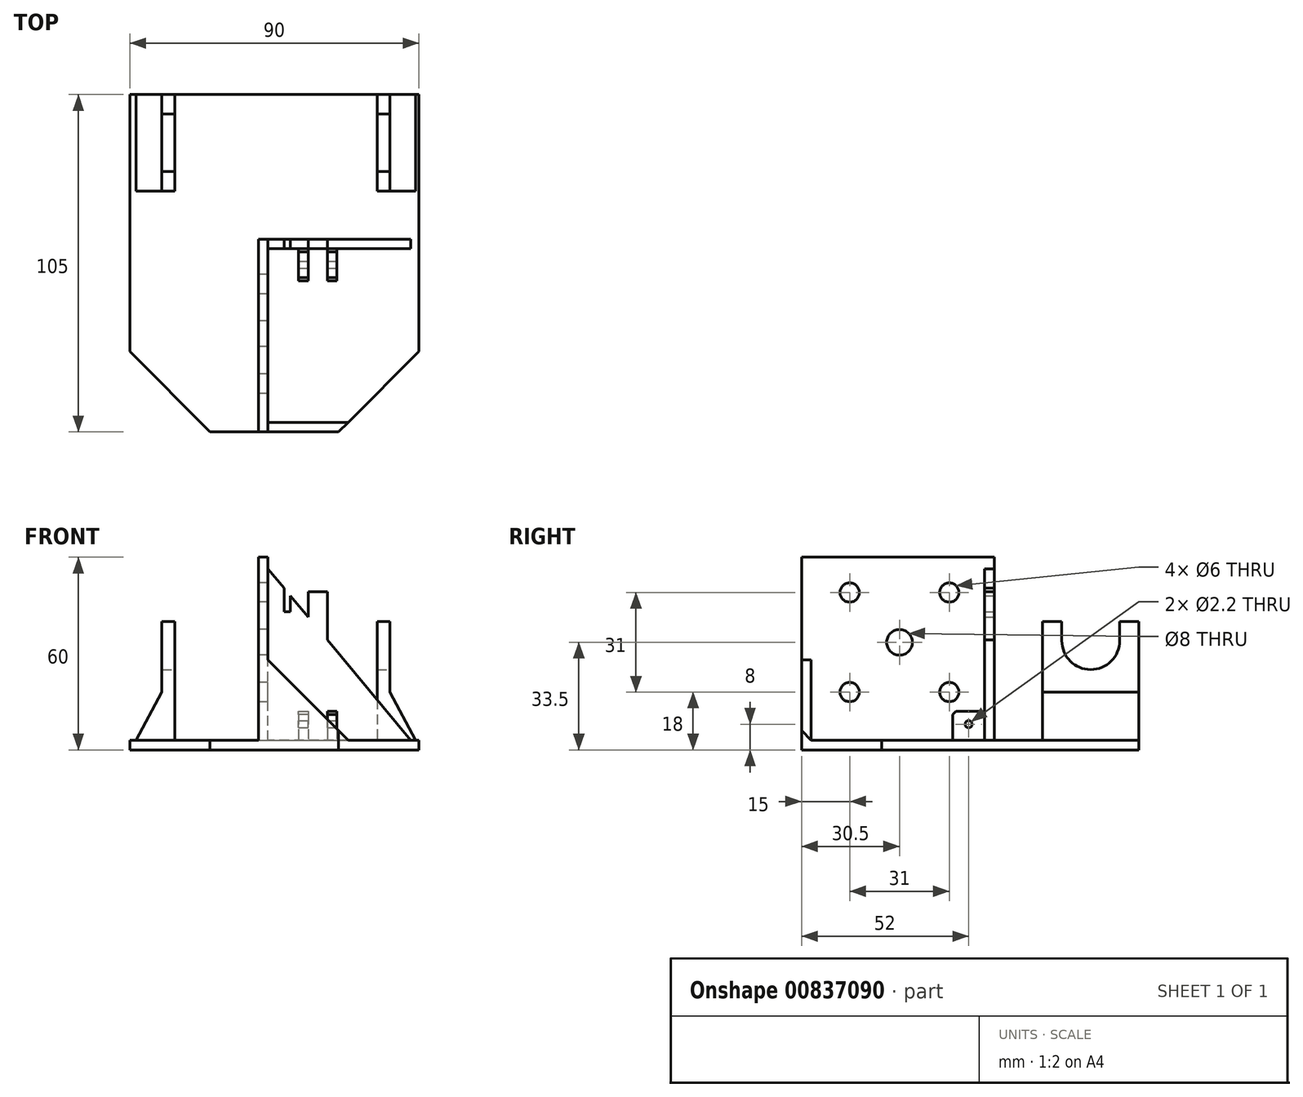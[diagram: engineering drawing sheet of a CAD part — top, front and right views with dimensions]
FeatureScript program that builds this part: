
annotation { "Feature Type Name" : "Feature", "Feature Type Description" : "" }
export const myFeature = defineFeature(function(context is Context, id is Id, definition is map)
    precondition{}
    {
        {
            var Q0;
            Q0=qCreatedBy(makeId("Top.planeOp"),FACE);
            var sketch = newSketch(context, id + "F0", { "sketchPlane" : qUnion([Q0])});
            skLineSegment(sketch, "E0.bottom", {"start": v(0, 0) * mm, "end": v(50, 0) * mm});
            skLineSegment(sketch, "E0.top", {"start": v(0, -60) * mm, "end": v(50, -60) * mm});
            skLineSegment(sketch, "E0.left", {"start": v(0, 0) * mm, "end": v(0, -60) * mm});
            skLineSegment(sketch, "E0.right", {"start": v(50, 0) * mm, "end": v(50, -60) * mm});
            skLineSegment(sketch, "E1.top", {"start": v(0, 45) * mm, "end": v(50, 45) * mm});
            skLineSegment(sketch, "E1.left", {"start": v(0, 0) * mm, "end": v(0, 45) * mm});
            skLineSegment(sketch, "E1.right", {"start": v(50, 0) * mm, "end": v(50, 45) * mm});
            skLineSegment(sketch, "E2.bottom", {"start": v(0, -60) * mm, "end": v(-40, -60) * mm});
            skLineSegment(sketch, "E2.top", {"start": v(0, 0) * mm, "end": v(-40, 0) * mm});
            skLineSegment(sketch, "E2.left", {"start": v(0, -60) * mm, "end": v(0, 0) * mm});
            skLineSegment(sketch, "E2.right", {"start": v(-40, -60) * mm, "end": v(-40, 0) * mm});
            skLineSegment(sketch, "E3.bottom", {"start": v(21.5, -3) * mm, "end": v(24.5, -3) * mm});
            skLineSegment(sketch, "E3.top", {"start": v(21.5, -13) * mm, "end": v(24.5, -13) * mm});
            skLineSegment(sketch, "E3.left", {"start": v(21.5, -3) * mm, "end": v(21.5, -13) * mm});
            skLineSegment(sketch, "E3.right", {"start": v(24.5, -3) * mm, "end": v(24.5, -13) * mm});
            skLineSegment(sketch, "E4.bottom", {"start": v(12.5, -3) * mm, "end": v(15.5, -3) * mm});
            skLineSegment(sketch, "E4.top", {"start": v(12.5, -13) * mm, "end": v(15.5, -13) * mm});
            skLineSegment(sketch, "E4.left", {"start": v(12.5, -3) * mm, "end": v(12.5, -13) * mm});
            skLineSegment(sketch, "E4.right", {"start": v(15.5, -3) * mm, "end": v(15.5, -13) * mm});
            skLineSegment(sketch, "E5", {"start": v(-40, 45) * mm, "end": v(-40, 0) * mm});
            skLineSegment(sketch, "E6", {"start": v(-40, 45) * mm, "end": v(0, 45) * mm});
            skLineSegment(sketch, "E7.bottom", {"start": v(-30, 45) * mm, "end": v(-26, 45) * mm});
            skLineSegment(sketch, "E7.top", {"start": v(-30, 15) * mm, "end": v(-26, 15) * mm});
            skLineSegment(sketch, "E7.left", {"start": v(-30, 45) * mm, "end": v(-30, 15) * mm});
            skLineSegment(sketch, "E7.right", {"start": v(-26, 45) * mm, "end": v(-26, 15) * mm});
            skLineSegment(sketch, "E8.bottom", {"start": v(37, 45) * mm, "end": v(41, 45) * mm});
            skLineSegment(sketch, "E8.top", {"start": v(37, 15) * mm, "end": v(41, 15) * mm});
            skLineSegment(sketch, "E8.left", {"start": v(37, 45) * mm, "end": v(37, 15) * mm});
            skLineSegment(sketch, "E8.right", {"start": v(41, 45) * mm, "end": v(41, 15) * mm});
            skSolve(sketch);
        }
        {
            var Q0;
            Q0=makeQuery(id+"F0.imprint","IMPRINT",FACE,{"disambiguationData":[TD([[makeQuery(id+"F0.imprint","IMPRINT",EDGE,{"derivedFrom":sQuery(id+"F0.wireOp",EDGE,"E0.left")}),-1.0]])]});
            var Q1;
            Q1=makeQuery(id+"F0.imprint","IMPRINT",FACE,{"disambiguationData":[TD([[makeQuery(id+"F0.imprint","IMPRINT",EDGE,{"derivedFrom":sQuery(id+"F0.wireOp",EDGE,"E0.bottom")}),-1.0]])]});
            var Q2;
            {var subQ1=sQuery(id+"F0.wireOp",EDGE,"48ikspD8-P3td-oRdJ-VHEi-jSUkpiZ7QIT4.bottom");Q2=makeQuery(id+"F0.imprint","IMPRINT",FACE,{"disambiguationData":[TD([[makeQuery(id+"F0.imprint","IMPRINT",EDGE,{"derivedFrom":subQ1}),-1.0]])]});}
            var Q3;
            Q3=makeQuery(id+"F0.imprint","IMPRINT",FACE,{"disambiguationData":[TD([[makeQuery(id+"F0.imprint","IMPRINT",EDGE,{"derivedFrom":sQuery(id+"F0.wireOp",EDGE,"E0.bottom")}),1.0]])]});
            var Q4;
            Q4=makeQuery(id+"F0.imprint","IMPRINT",FACE,{"disambiguationData":[TD([[makeQuery(id+"F0.imprint","IMPRINT",EDGE,{"derivedFrom":sQuery(id+"F0.wireOp",EDGE,"48ikspD8-P3td-oRdJ-VHEi-jSUkpiZ7QIT4.bottom")}),1.0]])]});
            var Q5;
            Q5=makeQuery(id+"F0.imprint","IMPRINT",FACE,{"disambiguationData":[TD([[makeQuery(id+"F0.imprint","IMPRINT",EDGE,{"derivedFrom":sQuery(id+"F0.wireOp",EDGE,"BPw0P3i8-2CSX-RIvv-VPia-wM2BSo4PSIyP.bottom")}),1.0]])]});
            var Q6;
            {var subQ2=sQuery(id+"F0.wireOp",EDGE,"BPw0P3i8-2CSX-RIvv-VPia-wM2BSo4PSIyP.bottom");Q6=makeQuery(id+"F0.imprint","IMPRINT",FACE,{"disambiguationData":[TD([[makeQuery(id+"F0.imprint","IMPRINT",EDGE,{"derivedFrom":subQ2}),-1.0]])]});}
            var Q7;
            {var subQ2=sQuery(id+"F0.wireOp",EDGE,"BPw0P3i8-2CSX-RIvv-VPia-wM2BSo4PSIyP.top");Q7=makeQuery(id+"F0.imprint","IMPRINT",FACE,{"disambiguationData":[TD([[makeQuery(id+"F0.imprint","IMPRINT",EDGE,{"derivedFrom":subQ2}),1.0]])]});}
            var Q8;
            {var subQ2=sQuery(id+"F0.wireOp",EDGE,"48ikspD8-P3td-oRdJ-VHEi-jSUkpiZ7QIT4.top");Q8=makeQuery(id+"F0.imprint","IMPRINT",FACE,{"disambiguationData":[TD([[makeQuery(id+"F0.imprint","IMPRINT",EDGE,{"derivedFrom":subQ2}),1.0]])]});}
            var Q9;
            {var subQ1=sQuery(id+"F0.wireOp",EDGE,"E1.left");Q9=makeQuery(id+"F0.imprint","IMPRINT",FACE,{"disambiguationData":[TD([[makeQuery(id+"F0.imprint","IMPRINT",EDGE,{"derivedFrom":subQ1}),1.0]])]});}
            extrude(context, id + "F1", {"entities" : qUnion([Q0, Q1, Q2, Q3, Q4, Q5, Q6, Q7, Q8, Q9]), "depth" : 3 * mm, "offsetDistance" : 25 * mm});
        }
        {
            var Q0;
            Q0=makeQuery(id+"F0.imprint","IMPRINT",FACE,{"disambiguationData":[TD([[makeQuery(id+"F0.imprint","IMPRINT",EDGE,{"derivedFrom":sQuery(id+"F0.wireOp",EDGE,"E7.top")}),1.0]])]});
            var Q1;
            Q1=makeQuery(id+"F0.imprint","IMPRINT",FACE,{"disambiguationData":[TD([[makeQuery(id+"F0.imprint","IMPRINT",EDGE,{"derivedFrom":sQuery(id+"F0.wireOp",EDGE,"E8.top")}),1.0]])]});
            extrude(context, id + "F2", {"entities" : qUnion([Q0, Q1]), "operationType" : NewBodyOperationType.ADD, "depth" : 40 * mm, "offsetDistance" : 25 * mm});
        }
        {
            var Q0;
            Q0=makeQuery(id+"F0.imprint","IMPRINT",FACE,{"disambiguationData":[TD([[makeQuery(id+"F0.imprint","IMPRINT",EDGE,{"derivedFrom":sQuery(id+"F0.wireOp",EDGE,"E3.bottom")}),-1.0]])]});
            var Q1;
            Q1=makeQuery(id+"F0.imprint","IMPRINT",FACE,{"disambiguationData":[TD([[makeQuery(id+"F0.imprint","IMPRINT",EDGE,{"derivedFrom":sQuery(id+"F0.wireOp",EDGE,"E4.bottom")}),-1.0]])]});
            extrude(context, id + "F3", {"entities" : qUnion([Q0, Q1]), "operationType" : NewBodyOperationType.ADD, "depth" : 12 * mm, "offsetDistance" : 25 * mm});
        }
        {
            var Q0;
            Q0=makeQuery(id+"F3.opExtrude","CAP_EDGE",EDGE,{"disambiguationData":[OSD([sQuery(id+"F0.wireOp",EDGE,"E4.bottom")])],"isStart":false});
            var Q1;
            Q1=makeQuery(id+"F3.opExtrude","CAP_EDGE",EDGE,{"disambiguationData":[OSD([sQuery(id+"F0.wireOp",EDGE,"E3.bottom")])],"isStart":false});
            var Q2;
            Q2=makeQuery(id+"F3.opExtrude","CAP_EDGE",EDGE,{"disambiguationData":[OSD([sQuery(id+"F0.wireOp",EDGE,"E3.top")])],"isStart":false});
            var Q3;
            Q3=makeQuery(id+"F3.opExtrude","CAP_EDGE",EDGE,{"disambiguationData":[OSD([sQuery(id+"F0.wireOp",EDGE,"E4.top")])],"isStart":false});
            chamfer(context, id + "F4", {"entities" : qUnion([Q0, Q1, Q2, Q3]), "width" : 1 * mm, "tangentPropagation" : true});
        }
        {
            var Q0;
            Q0=makeQuery(id+"F3.opExtrude","SWEPT_FACE",FACE,{"disambiguationData":[OSD([sQuery(id+"F0.wireOp",EDGE,"E3.right")])]});
            var sketch = newSketch(context, id + "F5", { "sketchPlane" : qUnion([Q0])});
            skCircle(sketch, "E9", {"center": v(-8, 8) * mm, "radius": 1.1 * mm});
            skSolve(sketch);
        }
        {
            var Q0;
            Q0=makeQuery(id+"F5.imprint","IMPRINT",FACE,{"disambiguationData":[TD([[makeQuery(id+"F5.imprint","IMPRINT",EDGE,{"derivedFrom":sQuery(id+"F5.wireOp",EDGE,"E9")}),1.0]])]});
            extrude(context, id + "F6", {"entities" : qUnion([Q0]), "operationType" : NewBodyOperationType.REMOVE, "oppositeDirection" : true, "depth" : 13 * mm, "offsetDistance" : 25 * mm});
        }
        {
            var Q0;
            Q0=qCreatedBy(makeId("Right.planeOp"),FACE);
            var sketch = newSketch(context, id + "F7", { "sketchPlane" : qUnion([Q0])});
            skLineSegment(sketch, "E10.bottom", {"start": v(0, 0) * mm, "end": v(-60, 0) * mm});
            skLineSegment(sketch, "E10.top", {"start": v(0, 60) * mm, "end": v(-60, 60) * mm});
            skLineSegment(sketch, "E10.left", {"start": v(0, 0) * mm, "end": v(0, 60) * mm});
            skLineSegment(sketch, "E10.right", {"start": v(-60, 0) * mm, "end": v(-60, 60) * mm});
            skCircle(sketch, "E11", {"center": v(-14, 49) * mm, "radius": 3 * mm});
            skCircle(sketch, "E12", {"center": v(-14, 18) * mm, "radius": 3 * mm});
            skCircle(sketch, "E13", {"center": v(-45, 49) * mm, "radius": 3 * mm});
            skCircle(sketch, "E14", {"center": v(-45, 18) * mm, "radius": 3 * mm});
            skLineSegment(sketch, "E15", {"start": v(-14, 49) * mm, "end": v(-45, 18) * mm, "construction": true});
            skPoint(sketch, "E16", {"position": v(-29.5, 33.5) * mm});
            skCircle(sketch, "E17", {"center": v(-29.5, 33.5) * mm, "radius": 4 * mm});
            skSolve(sketch);
        }
        {
            var Q0;
            {var subQ6=sQuery(id+"F7.wireOp",EDGE,"E10.bottom");Q0=makeQuery(id+"F7.imprint","IMPRINT",FACE,{"disambiguationData":[TD([[makeQuery(id+"F7.imprint","IMPRINT",EDGE,{"derivedFrom":subQ6}),-1.0]])]});}
            var Q1;
            {var subQ0=sQuery(id+"F7.wireOp",EDGE,"5ZiI2LFI-yI2u-3i1h-Rta8-WbluecZz7jaP");Q1=makeQuery(id+"F7.imprint","IMPRINT",FACE,{"disambiguationData":[TD([[makeQuery(id+"F7.imprint","IMPRINT",EDGE,{"derivedFrom":subQ0}),1.0]])]});}
            var Q2;
            {var subQ0=sQuery(id+"F7.wireOp",EDGE,"irvJjMzV-y1dr-gsLo-wSKk-gEWEVd7XGJBn");Q2=makeQuery(id+"F7.imprint","IMPRINT",FACE,{"disambiguationData":[TD([[makeQuery(id+"F7.imprint","IMPRINT",EDGE,{"derivedFrom":subQ0}),1.0]])]});}
            extrude(context, id + "F8", {"entities" : qUnion([Q0, Q1, Q2]), "operationType" : NewBodyOperationType.ADD, "depth" : 3 * mm, "offsetDistance" : 25 * mm});
        }
        {
            var Q0;
            Q0=qCreatedBy(makeId("Front.planeOp"),FACE);
            var sketch = newSketch(context, id + "F9", { "sketchPlane" : qUnion([Q0])});
            skLineSegment(sketch, "E18.bottom", {"start": v(0, 0) * mm, "end": v(50, 0) * mm});
            skLineSegment(sketch, "E18.left", {"start": v(0, 0) * mm, "end": v(0, 60) * mm});
            skLineSegment(sketch, "E19", {"start": v(50, 0) * mm, "end": v(0, 60) * mm});
            skLineSegment(sketch, "E20", {"start": v(15.5, 41.4) * mm, "end": v(15.5, 49.2) * mm});
            skLineSegment(sketch, "E21", {"start": v(15.5, 49.2) * mm, "end": v(21.5, 49.2) * mm});
            skLineSegment(sketch, "E22", {"start": v(21.5, 49.2) * mm, "end": v(21.5, 34.2) * mm});
            skLineSegment(sketch, "E23", {"start": v(8, 50.4) * mm, "end": v(8, 43) * mm});
            skLineSegment(sketch, "E24", {"start": v(8, 43) * mm, "end": v(10, 43) * mm});
            skLineSegment(sketch, "E25", {"start": v(10, 43) * mm, "end": v(10, 48) * mm});
            skSolve(sketch);
        }
        {
            var Q0;
            Q0=makeQuery(id+"F9.imprint","IMPRINT",FACE,{"disambiguationData":[TD([[makeQuery(id+"F9.imprint","IMPRINT",EDGE,{"derivedFrom":sQuery(id+"F9.wireOp",EDGE,"E18.bottom")}),1.0]])]});
            var Q1;
            {var subQ0=sQuery(id+"F9.wireOp",EDGE,"E20");Q1=makeQuery(id+"F9.imprint","IMPRINT",FACE,{"disambiguationData":[TD([[makeQuery(id+"F9.imprint","IMPRINT",EDGE,{"derivedFrom":subQ0}),-1.0]])]});}
            extrude(context, id + "F10", {"entities" : qUnion([Q0, Q1]), "operationType" : NewBodyOperationType.ADD, "depth" : 3 * mm, "offsetDistance" : 25 * mm});
        }
        {
            var Q0;
            Q0=makeQuery(id+"F2.opExtrude","SWEPT_FACE",FACE,{"disambiguationData":[OSD([sQuery(id+"F0.wireOp",EDGE,"E8.right")])]});
            var sketch = newSketch(context, id + "F11", { "sketchPlane" : qUnion([Q0])});
            skCircle(sketch, "E26", {"center": v(30, 34) * mm, "radius": 9 * mm});
            skLineSegment(sketch, "E27", {"start": v(39, 34) * mm, "end": v(39, 47) * mm});
            skLineSegment(sketch, "E28", {"start": v(21, 34) * mm, "end": v(21, 47) * mm});
            skLineSegment(sketch, "E29", {"start": v(39, 47) * mm, "end": v(21, 47) * mm});
            skSolve(sketch);
        }
        {
            var Q0;
            {var subQ0=sQuery(id+"F11.wireOp",EDGE,"E29");Q0=makeQuery(id+"F11.imprint","IMPRINT",FACE,{"disambiguationData":[TD([[makeQuery(id+"F11.imprint","IMPRINT",EDGE,{"derivedFrom":subQ0}),1.0]])]});}
            var Q1;
            {var subQ0=sQuery(id+"F11.wireOp",EDGE,"E26");var subQ1=makeQuery(id+"F11.imprint","INTERSECT",VERTEX,{"derivedFrom":[subQ0,sQuery(id+"F11.wireOp",EDGE,"E28")]});Q1=makeQuery(id+"F11.imprint","IMPRINT",FACE,{"disambiguationData":[TD([[makeQuery(id+"F11.imprint","IMPRINT",EDGE,{"disambiguationData":[TD([[subQ1,1.0]])],"derivedFrom":subQ0}),1.0]])]});}
            var Q2;
            {var subQ0=sQuery(id+"F11.wireOp",EDGE,"E26");var subQ1=makeQuery(id+"F2.opExtrude","CAP_EDGE",EDGE,{"disambiguationData":[OSD([sQuery(id+"F0.wireOp",EDGE,"E8.right")])],"isStart":false});var subQ2=makeQuery(id+"F11.imprint","INTERSECT",VERTEX,{"disambiguationData":[OD(0.0)],"derivedFrom":[subQ1,subQ0]});Q2=makeQuery(id+"F11.imprint","IMPRINT",FACE,{"disambiguationData":[TD([[makeQuery(id+"F11.imprint","IMPRINT",EDGE,{"disambiguationData":[TD([[subQ2,1.0]])],"derivedFrom":subQ0}),1.0]])]});}
            var Q3;
            {var subQ0=sQuery(id+"F11.wireOp",EDGE,"E28");var subQ1=sQuery(id+"F11.wireOp",EDGE,"E26");var subQ2=makeQuery(id+"F11.imprint","INTERSECT",VERTEX,{"derivedFrom":[subQ1,subQ0]});Q3=makeQuery(id+"F11.imprint","IMPRINT",FACE,{"disambiguationData":[TD([[makeQuery(id+"F11.imprint","IMPRINT",EDGE,{"disambiguationData":[TD([[subQ2,1.0]])],"derivedFrom":subQ1}),-1.0]])]});}
            var Q4;
            {var subQ0=sQuery(id+"F11.wireOp",EDGE,"E27");var subQ1=sQuery(id+"F11.wireOp",EDGE,"E26");var subQ2=makeQuery(id+"F11.imprint","INTERSECT",VERTEX,{"derivedFrom":[subQ1,subQ0]});Q4=makeQuery(id+"F11.imprint","IMPRINT",FACE,{"disambiguationData":[TD([[makeQuery(id+"F11.imprint","IMPRINT",EDGE,{"disambiguationData":[TD([[subQ2,-1.0]])],"derivedFrom":subQ1}),-1.0]])]});}
            extrude(context, id + "F12", {"entities" : qUnion([Q0, Q1, Q2, Q3, Q4]), "operationType" : NewBodyOperationType.REMOVE, "oppositeDirection" : true, "depth" : 100 * mm, "offsetDistance" : 25 * mm});
        }
        {
            var Q0;
            Q0=makeQuery(id+"F8.boolean.opBoolean","MERGE",FACE,{"derivedFrom":[makeQuery(id+"F1.opExtrude","SWEPT_FACE",FACE,{"disambiguationData":[OSD([sQuery(id+"F0.wireOp",EDGE,"E0.top"),sQuery(id+"F0.wireOp",EDGE,"E2.bottom")])]}),makeQuery(id+"F8.opExtrude","SWEPT_FACE",FACE,{"disambiguationData":[OSD([sQuery(id+"F7.wireOp",EDGE,"E10.right")])]})]});
            var sketch = newSketch(context, id + "F13", { "sketchPlane" : qUnion([Q0])});
            skLineSegment(sketch, "E30", {"start": v(3, 3) * mm, "end": v(3, 28) * mm});
            skLineSegment(sketch, "E31", {"start": v(3, 28) * mm, "end": v(28, 3) * mm});
            skLineSegment(sketch, "E32", {"start": v(28, 3) * mm, "end": v(3, 3) * mm});
            skSolve(sketch);
        }
        {
            var Q0;
            Q0=makeQuery(id+"F13.imprint","IMPRINT",FACE,{"disambiguationData":[TD([[makeQuery(id+"F13.imprint","IMPRINT",EDGE,{"derivedFrom":sQuery(id+"F13.wireOp",EDGE,"E30")}),-1.0]])]});
            extrude(context, id + "F14", {"entities" : qUnion([Q0]), "operationType" : NewBodyOperationType.ADD, "oppositeDirection" : true, "depth" : 3 * mm, "offsetDistance" : 25 * mm});
        }
        {
            var Q0;
            Q0=makeQuery(id+"F1.opExtrude","SWEPT_EDGE",EDGE,{"disambiguationData":[OSD([sQuery(id+"F0.wireOp",EDGE,"E0.top"),sQuery(id+"F0.wireOp",EDGE,"E0.right")])]});
            var Q1;
            Q1=makeQuery(id+"F1.opExtrude","SWEPT_EDGE",EDGE,{"disambiguationData":[OSD([sQuery(id+"F0.wireOp",EDGE,"E2.bottom"),sQuery(id+"F0.wireOp",EDGE,"E2.right")])]});
            chamfer(context, id + "F15", {"entities" : qUnion([Q0, Q1]), "width" : 25 * mm, "tangentPropagation" : true});
        }
        {
            var Q0;
            {var subQ0=sQuery(id+"F0.wireOp",EDGE,"E6");var subQ1=sQuery(id+"F0.wireOp",EDGE,"E1.top");Q0=makeQuery(id+"F2.boolean.opBoolean","MERGE",FACE,{"derivedFrom":[makeQuery(id+"F1.opExtrude","SWEPT_FACE",FACE,{"disambiguationData":[OSD([subQ1,subQ0])]}),makeQuery(id+"F1.opExtrude","SWEPT_FACE",FACE,{"disambiguationData":[OSD([subQ1])]}),makeQuery(id+"F1.opExtrude","SWEPT_FACE",FACE,{"disambiguationData":[OSD([subQ0])]}),makeQuery(id+"F2.opExtrude","SWEPT_FACE",FACE,{"disambiguationData":[OSD([subQ1])]}),makeQuery(id+"F2.opExtrude","SWEPT_FACE",FACE,{"disambiguationData":[OSD([subQ0])]})]});}
            var sketch = newSketch(context, id + "F16", { "sketchPlane" : qUnion([Q0])});
            skPoint(sketch, "E33.0", {"position": v(-41, 3) * mm});
            skPoint(sketch, "E33.1", {"position": v(30, 3) * mm});
            skLineSegment(sketch, "E34", {"start": v(-41, 3) * mm, "end": v(-41, 18) * mm});
            skLineSegment(sketch, "E35", {"start": v(-41, 18) * mm, "end": v(-49, 3) * mm});
            skLineSegment(sketch, "E36", {"start": v(-49, 3) * mm, "end": v(-41, 3) * mm});
            skLineSegment(sketch, "E37", {"start": v(30, 3) * mm, "end": v(30, 18) * mm});
            skLineSegment(sketch, "E38", {"start": v(30, 18) * mm, "end": v(38, 3) * mm});
            skLineSegment(sketch, "E39", {"start": v(38, 3) * mm, "end": v(30, 3) * mm});
            skSolve(sketch);
        }
        {
            var Q0;
            Q0=makeQuery(id+"F16.imprint","IMPRINT",FACE,{"disambiguationData":[TD([[makeQuery(id+"F16.imprint","IMPRINT",EDGE,{"derivedFrom":sQuery(id+"F16.wireOp",EDGE,"E37")}),1.0]])]});
            var Q1;
            Q1=makeQuery(id+"F16.imprint","IMPRINT",FACE,{"disambiguationData":[TD([[makeQuery(id+"F16.imprint","IMPRINT",EDGE,{"derivedFrom":sQuery(id+"F16.wireOp",EDGE,"E34")}),-1.0]])]});
            extrude(context, id + "F17", {"entities" : qUnion([Q0, Q1]), "operationType" : NewBodyOperationType.ADD, "oppositeDirection" : true, "depth" : 30 * mm, "offsetDistance" : 25 * mm});
        }
    });
